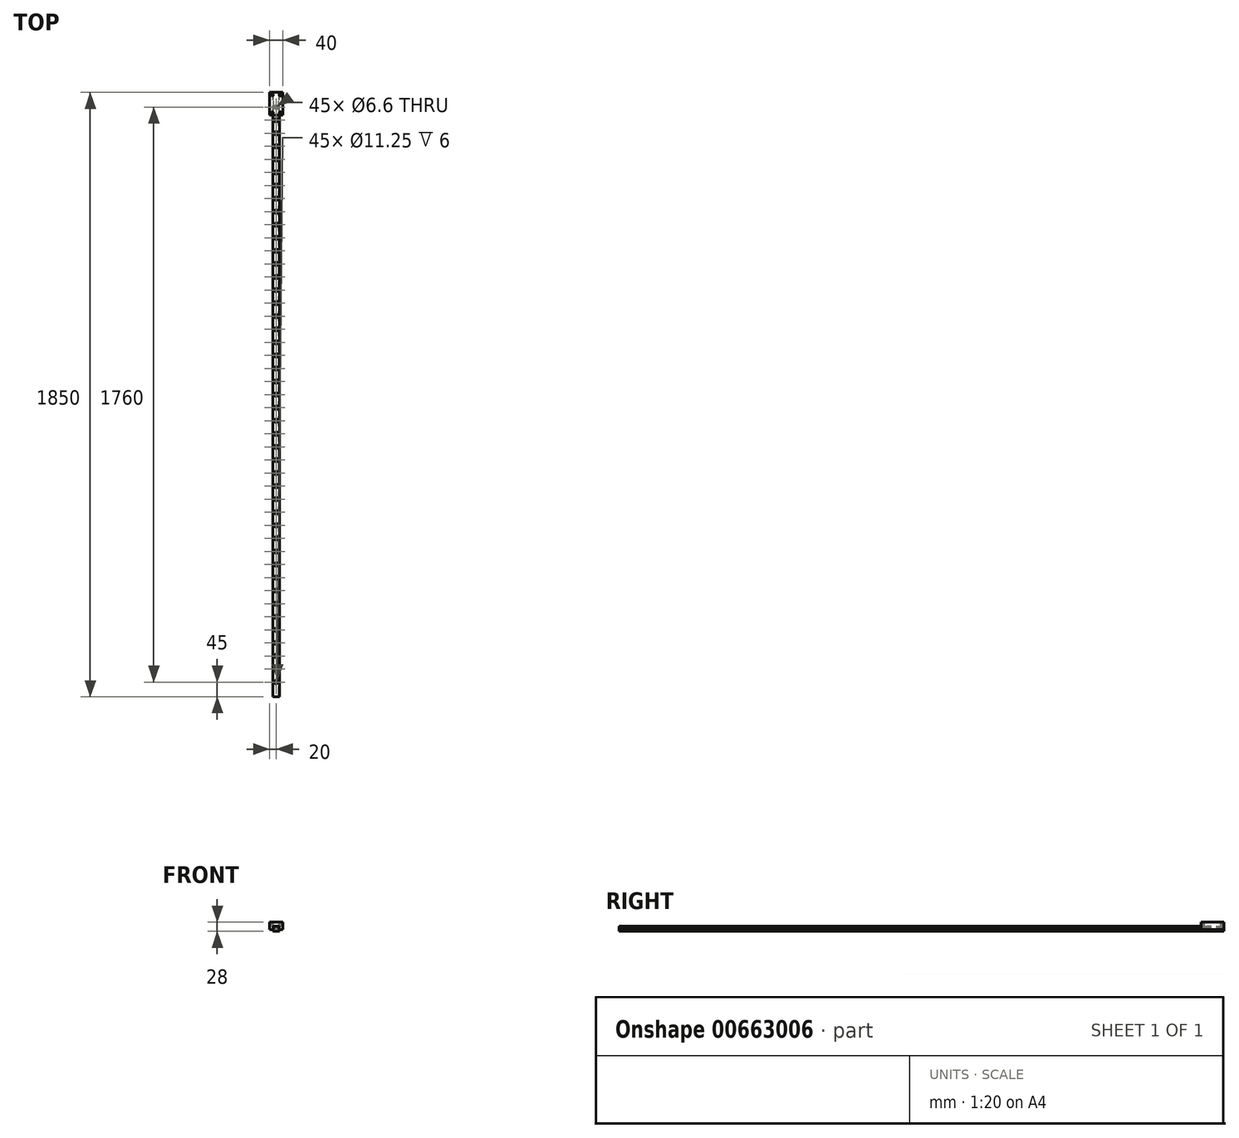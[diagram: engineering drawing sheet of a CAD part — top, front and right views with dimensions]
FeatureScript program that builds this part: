
annotation { "Feature Type Name" : "Feature", "Feature Type Description" : "" }
export const myFeature = defineFeature(function(context is Context, id is Id, definition is map)
    precondition{}
    {
        {
            var Q0;
            Q0=qCreatedBy(makeId("Front.planeOp"),FACE);
            var sketch = newSketch(context, id + "F0", { "sketchPlane" : qUnion([Q0])});
            skLineSegment(sketch, "E0", {"start": v(0, 0) * mm, "end": v(-10, 0) * mm});
            skLineSegment(sketch, "E1", {"start": v(-10, 0) * mm, "end": v(-10, -2) * mm});
            skLineSegment(sketch, "E2", {"start": v(-10, -2) * mm, "end": v(-8, -4) * mm});
            skLineSegment(sketch, "E3", {"start": v(-8, -4) * mm, "end": v(-8, -7) * mm});
            skLineSegment(sketch, "E4", {"start": v(-8, -7) * mm, "end": v(-10, -9) * mm});
            skLineSegment(sketch, "E5", {"start": v(-10, -9) * mm, "end": v(-10, -15.5) * mm});
            skLineSegment(sketch, "E6", {"start": v(-10, -15.5) * mm, "end": v(0, -15.5) * mm});
            skLineSegment(sketch, "E7", {"start": v(0, -15.5) * mm, "end": v(10, -15.5) * mm});
            skLineSegment(sketch, "E8", {"start": v(10, -15.5) * mm, "end": v(10, -9) * mm});
            skLineSegment(sketch, "E9", {"start": v(10, -9) * mm, "end": v(8, -7) * mm});
            skLineSegment(sketch, "E10", {"start": v(8, -7) * mm, "end": v(8, -4) * mm});
            skLineSegment(sketch, "E11", {"start": v(8, -4) * mm, "end": v(10, -2) * mm});
            skLineSegment(sketch, "E12", {"start": v(10, -2) * mm, "end": v(10, 0) * mm});
            skLineSegment(sketch, "E13", {"start": v(10, 0) * mm, "end": v(0, 0) * mm});
            skLineSegment(sketch, "E14", {"start": v(10, -10) * mm, "end": v(20, -10) * mm});
            skLineSegment(sketch, "E15", {"start": v(20, -10) * mm, "end": v(20, 12.5) * mm});
            skLineSegment(sketch, "E16", {"start": v(20, 12.5) * mm, "end": v(-20, 12.5) * mm});
            skLineSegment(sketch, "E17", {"start": v(-20, 12.5) * mm, "end": v(-20, -10) * mm});
            skLineSegment(sketch, "E18", {"start": v(-20, -10) * mm, "end": v(-10, -10) * mm});
            skLineSegment(sketch, "E19", {"start": v(8.5, -3.5) * mm, "end": v(8.5, -7.5) * mm});
            skLineSegment(sketch, "E20", {"start": v(-8.5, -3.5) * mm, "end": v(-8.5, -7.5) * mm});
            skSolve(sketch);
        }
        {
            var Q0;
            Q0=makeQuery(id+"F0.imprint","IMPRINT",FACE,{"disambiguationData":[TD([[makeQuery(id+"F0.imprint","IMPRINT",EDGE,{"derivedFrom":sQuery(id+"F0.wireOp",EDGE,"E0")}),1.0]])]});
            extrude(context, id + "F1", {"entities" : qUnion([Q0]), "depth" : 1850 * mm, "offsetDistance" : 25 * mm});
        }
        {
            var Q0;
            Q0=makeQuery(id+"F1.opExtrude","SWEPT_FACE",FACE,{"disambiguationData":[OSD([sQuery(id+"F0.wireOp",EDGE,"E0"),sQuery(id+"F0.wireOp",EDGE,"E13")])]});
            var sketch = newSketch(context, id + "F2", { "sketchPlane" : qUnion([Q0])});
            skPoint(sketch, "E21", {"position": v(0, -45) * mm});
            skPoint(sketch, "E22.0.1.0", {"position": v(0, -85) * mm});
            skPoint(sketch, "E22.0.2.0", {"position": v(0, -125) * mm});
            skPoint(sketch, "E22.0.3.0", {"position": v(0, -165) * mm});
            skPoint(sketch, "E22.0.4.0", {"position": v(0, -205) * mm});
            skPoint(sketch, "E22.0.5.0", {"position": v(0, -245) * mm});
            skPoint(sketch, "E22.0.6.0", {"position": v(0, -285) * mm});
            skPoint(sketch, "E22.0.7.0", {"position": v(0, -325) * mm});
            skPoint(sketch, "E22.0.8.0", {"position": v(0, -365) * mm});
            skPoint(sketch, "E22.0.9.0", {"position": v(0, -405) * mm});
            skPoint(sketch, "E22.0.10.0", {"position": v(0, -445) * mm});
            skPoint(sketch, "E22.0.11.0", {"position": v(0, -485) * mm});
            skPoint(sketch, "E22.0.12.0", {"position": v(0, -525) * mm});
            skPoint(sketch, "E22.0.13.0", {"position": v(0, -565) * mm});
            skPoint(sketch, "E22.0.14.0", {"position": v(0, -605) * mm});
            skPoint(sketch, "E22.0.15.0", {"position": v(0, -645) * mm});
            skPoint(sketch, "E22.0.16.0", {"position": v(0, -685) * mm});
            skPoint(sketch, "E22.0.17.0", {"position": v(0, -725) * mm});
            skPoint(sketch, "E22.0.18.0", {"position": v(0, -765) * mm});
            skPoint(sketch, "E22.0.19.0", {"position": v(0, -805) * mm});
            skLineSegment(sketch, "E22.direction1", {"start": v(0, -45) * mm, "end": v(25, -45) * mm, "construction": true});
            skLineSegment(sketch, "E22.direction2", {"start": v(0, -45) * mm, "end": v(0, -85) * mm, "construction": true});
            skPoint(sketch, "E23.0.0.20", {"position": v(0, -845) * mm});
            skPoint(sketch, "E23.0.0.21", {"position": v(0, -885) * mm});
            skPoint(sketch, "E23.0.0.22", {"position": v(0, -925) * mm});
            skPoint(sketch, "E23.0.0.23", {"position": v(0, -965) * mm});
            skPoint(sketch, "E23.0.0.24", {"position": v(0, -1005) * mm});
            skPoint(sketch, "E23.0.0.25", {"position": v(0, -1045) * mm});
            skPoint(sketch, "E23.0.0.26", {"position": v(0, -1085) * mm});
            skPoint(sketch, "E23.0.0.27", {"position": v(0, -1125) * mm});
            skPoint(sketch, "E23.0.0.28", {"position": v(0, -1165) * mm});
            skPoint(sketch, "E23.0.0.29", {"position": v(0, -1205) * mm});
            skPoint(sketch, "E23.0.0.30", {"position": v(0, -1245) * mm});
            skPoint(sketch, "E23.0.0.31", {"position": v(0, -1285) * mm});
            skPoint(sketch, "E23.0.0.32", {"position": v(0, -1325) * mm});
            skPoint(sketch, "E23.0.0.33", {"position": v(0, -1365) * mm});
            skPoint(sketch, "E23.0.0.34", {"position": v(0, -1405) * mm});
            skPoint(sketch, "E23.0.0.35", {"position": v(0, -1445) * mm});
            skPoint(sketch, "E23.0.0.36", {"position": v(0, -1485) * mm});
            skPoint(sketch, "E23.0.0.37", {"position": v(0, -1525) * mm});
            skPoint(sketch, "E23.0.0.38", {"position": v(0, -1565) * mm});
            skPoint(sketch, "E23.0.0.39", {"position": v(0, -1605) * mm});
            skPoint(sketch, "E24.0.0.40", {"position": v(0, -1645) * mm});
            skPoint(sketch, "E24.0.0.41", {"position": v(0, -1685) * mm});
            skPoint(sketch, "E24.0.0.42", {"position": v(0, -1725) * mm});
            skPoint(sketch, "E24.0.0.43", {"position": v(0, -1765) * mm});
            skPoint(sketch, "E25.0.0.44", {"position": v(0, -1805) * mm});
            skSolve(sketch);
        }
        {
            var Q0;
            Q0=sQuery(id+"F2.wireOp",VERTEX,"E25.0.0.44");
            var Q1;
            Q1=sQuery(id+"F2.wireOp",VERTEX,"E24.0.0.43");
            var Q2;
            Q2=sQuery(id+"F2.wireOp",VERTEX,"E24.0.0.42");
            var Q3;
            Q3=sQuery(id+"F2.wireOp",VERTEX,"E24.0.0.41");
            var Q4;
            Q4=sQuery(id+"F2.wireOp",VERTEX,"E24.0.0.40");
            var Q5;
            Q5=sQuery(id+"F2.wireOp",VERTEX,"E23.0.0.39");
            var Q6;
            Q6=sQuery(id+"F2.wireOp",VERTEX,"E23.0.0.38");
            var Q7;
            Q7=sQuery(id+"F2.wireOp",VERTEX,"E23.0.0.37");
            var Q8;
            Q8=sQuery(id+"F2.wireOp",VERTEX,"E23.0.0.36");
            var Q9;
            Q9=sQuery(id+"F2.wireOp",VERTEX,"E23.0.0.35");
            var Q10;
            Q10=sQuery(id+"F2.wireOp",VERTEX,"E23.0.0.34");
            var Q11;
            Q11=sQuery(id+"F2.wireOp",VERTEX,"E23.0.0.33");
            var Q12;
            Q12=sQuery(id+"F2.wireOp",VERTEX,"E23.0.0.32");
            var Q13;
            Q13=sQuery(id+"F2.wireOp",VERTEX,"E23.0.0.31");
            var Q14;
            Q14=sQuery(id+"F2.wireOp",VERTEX,"E23.0.0.30");
            var Q15;
            Q15=sQuery(id+"F2.wireOp",VERTEX,"E23.0.0.29");
            var Q16;
            Q16=sQuery(id+"F2.wireOp",VERTEX,"E23.0.0.28");
            var Q17;
            Q17=sQuery(id+"F2.wireOp",VERTEX,"E23.0.0.27");
            var Q18;
            Q18=sQuery(id+"F2.wireOp",VERTEX,"E23.0.0.26");
            var Q19;
            Q19=sQuery(id+"F2.wireOp",VERTEX,"E23.0.0.25");
            var Q20;
            Q20=sQuery(id+"F2.wireOp",VERTEX,"E23.0.0.24");
            var Q21;
            Q21=sQuery(id+"F2.wireOp",VERTEX,"E23.0.0.23");
            var Q22;
            Q22=sQuery(id+"F2.wireOp",VERTEX,"E23.0.0.22");
            var Q23;
            Q23=sQuery(id+"F2.wireOp",VERTEX,"E23.0.0.21");
            var Q24;
            Q24=sQuery(id+"F2.wireOp",VERTEX,"E23.0.0.20");
            var Q25;
            Q25=sQuery(id+"F2.wireOp",VERTEX,"E22.0.19.0");
            var Q26;
            Q26=sQuery(id+"F2.wireOp",VERTEX,"E22.0.18.0");
            var Q27;
            Q27=sQuery(id+"F2.wireOp",VERTEX,"E22.0.17.0");
            var Q28;
            Q28=sQuery(id+"F2.wireOp",VERTEX,"E22.0.16.0");
            var Q29;
            Q29=sQuery(id+"F2.wireOp",VERTEX,"E22.0.15.0");
            var Q30;
            Q30=sQuery(id+"F2.wireOp",VERTEX,"E22.0.14.0");
            var Q31;
            Q31=sQuery(id+"F2.wireOp",VERTEX,"E22.0.13.0");
            var Q32;
            Q32=sQuery(id+"F2.wireOp",VERTEX,"E22.0.12.0");
            var Q33;
            Q33=sQuery(id+"F2.wireOp",VERTEX,"E22.0.11.0");
            var Q34;
            Q34=sQuery(id+"F2.wireOp",VERTEX,"E22.0.10.0");
            var Q35;
            Q35=sQuery(id+"F2.wireOp",VERTEX,"E22.0.9.0");
            var Q36;
            Q36=sQuery(id+"F2.wireOp",VERTEX,"E22.0.8.0");
            var Q37;
            Q37=sQuery(id+"F2.wireOp",VERTEX,"E22.0.7.0");
            var Q38;
            Q38=sQuery(id+"F2.wireOp",VERTEX,"E22.0.6.0");
            var Q39;
            Q39=sQuery(id+"F2.wireOp",VERTEX,"E22.0.5.0");
            var Q40;
            Q40=sQuery(id+"F2.wireOp",VERTEX,"E22.0.4.0");
            var Q41;
            Q41=sQuery(id+"F2.wireOp",VERTEX,"E22.0.3.0");
            var Q42;
            Q42=sQuery(id+"F2.wireOp",VERTEX,"E22.0.2.0");
            var Q43;
            Q43=sQuery(id+"F2.wireOp",VERTEX,"E22.0.1.0");
            var Q44;
            Q44=sQuery(id+"F2.wireOp",VERTEX,"E21");
            var Q45;
            Q45=makeQuery(id+"F1.opExtrude","SWEPT_BODY",BODY,{"disambiguationData":[OSD([sQuery(id+"F0.wireOp",EDGE,"E0"),sQuery(id+"F0.wireOp",EDGE,"E1"),sQuery(id+"F0.wireOp",EDGE,"E2"),sQuery(id+"F0.wireOp",EDGE,"E3"),sQuery(id+"F0.wireOp",EDGE,"E4"),sQuery(id+"F0.wireOp",EDGE,"E5"),sQuery(id+"F0.wireOp",EDGE,"E6"),sQuery(id+"F0.wireOp",EDGE,"E7"),sQuery(id+"F0.wireOp",EDGE,"E8"),sQuery(id+"F0.wireOp",EDGE,"E9"),sQuery(id+"F0.wireOp",EDGE,"E10"),sQuery(id+"F0.wireOp",EDGE,"E11"),sQuery(id+"F0.wireOp",EDGE,"E12"),sQuery(id+"F0.wireOp",EDGE,"E13")])]});
            hole(context, id + "F3", {"style" : HoleStyle.C_BORE, "endStyle" : HoleEndStyle.THROUGH, "standardTappedOrClearance" : lookupTablePath({ "fit" : "Normal", "standard" : "ISO", "size" : "M6", "type" : "Clearance" }), "standardBlindInLast" : lookupTablePath({ "fit" : "Normal", "standard" : "ISO", "engagement" : "75%", "pitch" : "1 mm", "size" : "M6", "type" : "Clearance & tapped" }), "holeDiameter" : 6.6 * mm, "cBoreDiameter" : 11.25 * mm, "cBoreDepth" : 6 * mm, "majorDiameter" : 5 * mm, "isTappedThrough" : true, "tappedDepth" : 12 * mm, "tapClearance" : 3, "locations" : qUnion([Q0, Q1, Q2, Q3, Q4, Q5, Q6, Q7, Q8, Q9, Q10, Q11, Q12, Q13, Q14, Q15, Q16, Q17, Q18, Q19, Q20, Q21, Q22, Q23, Q24, Q25, Q26, Q27, Q28, Q29, Q30, Q31, Q32, Q33, Q34, Q35, Q36, Q37, Q38, Q39, Q40, Q41, Q42, Q43, Q44]), "scope" : qUnion([Q45])});
        }
        {
            var Q0;
            Q0=makeQuery(id+"F0.imprint","IMPRINT",FACE,{"disambiguationData":[TD([[makeQuery(id+"F0.imprint","IMPRINT",EDGE,{"derivedFrom":sQuery(id+"F0.wireOp",EDGE,"E0")}),-1.0]])]});
            extrude(context, id + "F4", {"entities" : qUnion([Q0]), "depth" : 70 * mm, "offsetDistance" : 25 * mm});
        }
        {
            var Q0;
            Q0=makeQuery(id+"F4.opExtrude","SWEPT_FACE",FACE,{"disambiguationData":[OSD([sQuery(id+"F0.wireOp",EDGE,"E16")])]});
            var sketch = newSketch(context, id + "F5", { "sketchPlane" : qUnion([Q0])});
            skLineSegment(sketch, "E26.bottom", {"start": v(-12, -8) * mm, "end": v(12, -8) * mm, "construction": true});
            skLineSegment(sketch, "E26.top", {"start": v(-12, -62) * mm, "end": v(12, -62) * mm, "construction": true});
            skLineSegment(sketch, "E26.left", {"start": v(-12, -8) * mm, "end": v(-12, -62) * mm, "construction": true});
            skLineSegment(sketch, "E26.right", {"start": v(12, -8) * mm, "end": v(12, -62) * mm, "construction": true});
            skPoint(sketch, "E27", {"position": v(-12, -8) * mm});
            skPoint(sketch, "E28", {"position": v(12, -8) * mm});
            skPoint(sketch, "E29", {"position": v(12, -62) * mm});
            skPoint(sketch, "E30", {"position": v(-12, -62) * mm});
            skSolve(sketch);
        }
        {
            var Q0;
            Q0=sQuery(id+"F5.wireOp",VERTEX,"E27");
            var Q1;
            Q1=sQuery(id+"F5.wireOp",VERTEX,"E28");
            var Q2;
            Q2=sQuery(id+"F5.wireOp",VERTEX,"E29");
            var Q3;
            Q3=sQuery(id+"F5.wireOp",VERTEX,"E30");
            var Q4;
            Q4=makeQuery(id+"F4.opExtrude","SWEPT_BODY",BODY,{"disambiguationData":[OSD([sQuery(id+"F0.wireOp",EDGE,"E0"),sQuery(id+"F0.wireOp",EDGE,"E1"),sQuery(id+"F0.wireOp",EDGE,"E2"),sQuery(id+"F0.wireOp",EDGE,"E4"),sQuery(id+"F0.wireOp",EDGE,"E5"),sQuery(id+"F0.wireOp",EDGE,"E8"),sQuery(id+"F0.wireOp",EDGE,"E9"),sQuery(id+"F0.wireOp",EDGE,"E11"),sQuery(id+"F0.wireOp",EDGE,"E12"),sQuery(id+"F0.wireOp",EDGE,"E13"),sQuery(id+"F0.wireOp",EDGE,"E14"),sQuery(id+"F0.wireOp",EDGE,"E15"),sQuery(id+"F0.wireOp",EDGE,"E16"),sQuery(id+"F0.wireOp",EDGE,"E17"),sQuery(id+"F0.wireOp",EDGE,"E18"),sQuery(id+"F0.wireOp",EDGE,"E19"),sQuery(id+"F0.wireOp",EDGE,"E20")])]});
            hole(context, id + "F6", {"style" : HoleStyle.SIMPLE, "endStyle" : HoleEndStyle.BLIND, "standardTappedOrClearance" : lookupTablePath({ "fit" : "Normal", "standard" : "ISO", "size" : "M5", "type" : "Clearance" }), "standardBlindInLast" : lookupTablePath({ "fit" : "Normal", "standard" : "ISO", "engagement" : "75%", "pitch" : "0.8 mm", "size" : "M5", "type" : "Clearance & tapped" }), "holeDiameter" : 5.5 * mm, "majorDiameter" : 5 * mm, "holeDepth" : 9 * mm, "isTappedThrough" : true, "tappedDepth" : 12 * mm, "tapClearance" : 3, "locations" : qUnion([Q0, Q1, Q2, Q3]), "scope" : qUnion([Q4])});
        }
    });
